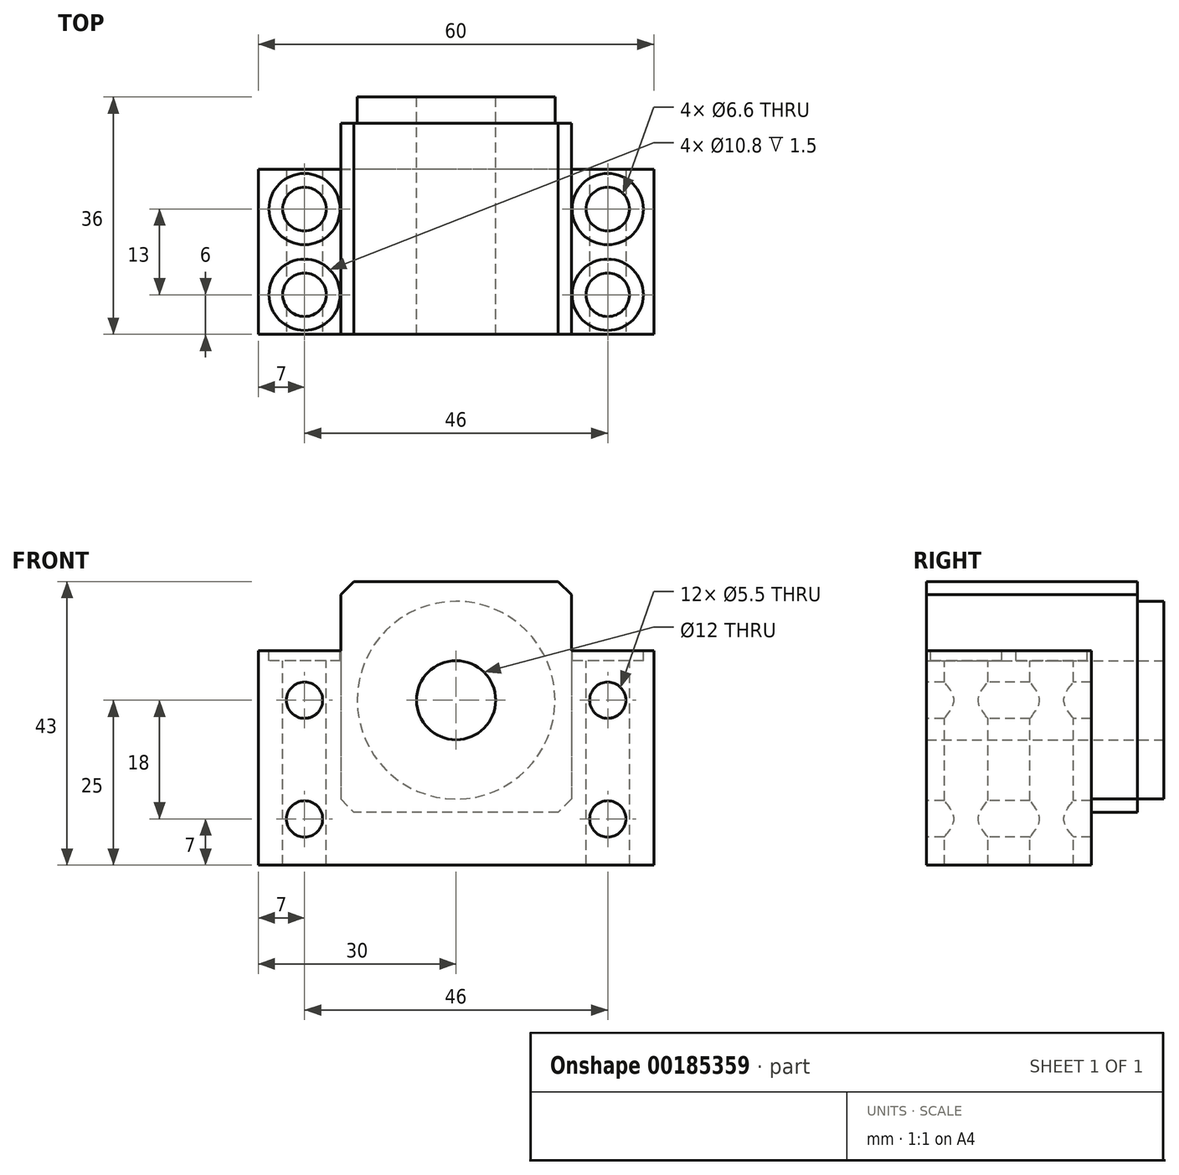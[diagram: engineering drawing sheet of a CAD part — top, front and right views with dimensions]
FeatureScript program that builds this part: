
annotation { "Feature Type Name" : "Feature", "Feature Type Description" : "" }
export const myFeature = defineFeature(function(context is Context, id is Id, definition is map)
    precondition{}
    {
        {
            var Q0;
            Q0=qCreatedBy(makeId("Front.planeOp"),FACE);
            var sketch = newSketch(context, id + "F8", { "sketchPlane" : qUnion([Q0])});
            skLineSegment(sketch, "E0.bottom", {"start": v(30, 16.25) * mm, "end": v(-30, 16.25) * mm});
            skLineSegment(sketch, "E0.top", {"start": v(30, -16.25) * mm, "end": v(-30, -16.25) * mm});
            skLineSegment(sketch, "E0.left", {"start": v(30, 16.25) * mm, "end": v(30, -16.25) * mm});
            skLineSegment(sketch, "E0.right", {"start": v(-30, 16.25) * mm, "end": v(-30, -16.25) * mm});
            skPoint(sketch, "E0.middle", {"position": v(0, 0) * mm});
            skSolve(sketch);
        }
        {
            var Q0;
            Q0=makeQuery(id+"F8.imprint","IMPRINT",FACE,{"disambiguationData":[TD([[makeQuery(id+"F8.imprint","IMPRINT",EDGE,{"derivedFrom":sQuery(id+"F8.wireOp",EDGE,"E0.bottom")}),1.0]])]});
            extrude(context, id + "F9", {"entities" : qUnion([Q0]), "oppositeDirection" : true, "depth" : 25 * mm});
        }
        {
            var Q0;
            Q0=qCreatedBy(makeId("Front.planeOp"),FACE);
            var sketch = newSketch(context, id + "F0", { "sketchPlane" : qUnion([Q0])});
            skLineSegment(sketch, "E1.bottom", {"start": v(17.5, 26.75) * mm, "end": v(-17.5, 26.75) * mm});
            skLineSegment(sketch, "E1.top", {"start": v(17.5, -8.25) * mm, "end": v(-17.5, -8.25) * mm});
            skLineSegment(sketch, "E1.left", {"start": v(17.5, 26.75) * mm, "end": v(17.5, -8.25) * mm});
            skLineSegment(sketch, "E1.right", {"start": v(-17.5, 26.75) * mm, "end": v(-17.5, -8.25) * mm});
            skPoint(sketch, "E1.middle", {"position": v(0, 9.25) * mm});
            skSolve(sketch);
        }
        {
            var Q0;
            Q0=makeQuery(id+"F0.imprint","IMPRINT",FACE,{"disambiguationData":[TD([[makeQuery(id+"F0.imprint","IMPRINT",EDGE,{"derivedFrom":sQuery(id+"F0.wireOp",EDGE,"E1.bottom")}),1.0]])]});
            extrude(context, id + "F10", {"entities" : qUnion([Q0]), "operationType" : NewBodyOperationType.ADD, "oppositeDirection" : true, "depth" : 32 * mm});
        }
        {
            var Q0;
            Q0=makeQuery(id+"F10.opExtrude","CAP_FACE",FACE,{"disambiguationData":[OSD([sQuery(id+"F0.wireOp",EDGE,"E1.bottom"),sQuery(id+"F0.wireOp",EDGE,"E1.top"),sQuery(id+"F0.wireOp",EDGE,"E1.left"),sQuery(id+"F0.wireOp",EDGE,"E1.right")])],"isStart":false});
            var sketch = newSketch(context, id + "F1", { "sketchPlane" : qUnion([Q0])});
            skCircle(sketch, "E2", {"center": v(0, 8.75) * mm, "radius": 6 * mm});
            skSolve(sketch);
        }
        {
            var Q0;
            Q0=makeQuery(id+"F1.imprint","IMPRINT",FACE,{"disambiguationData":[TD([[makeQuery(id+"F1.imprint","IMPRINT",EDGE,{"derivedFrom":sQuery(id+"F1.wireOp",EDGE,"E2")}),1.0]])]});
            var Q1;
            Q1=sQuery(id+"F1.wireOp",EDGE,"E2");
            extrude(context, id + "F11", {"entities" : qUnion([Q0]), "operationType" : NewBodyOperationType.REMOVE, "surfaceEntities" : qUnion([Q1]), "endBound" : BoundingType.THROUGH_ALL, "oppositeDirection" : true, "depth" : 25 * mm});
        }
        {
            var Q0;
            Q0=makeQuery(id+"F10.opExtrude","SWEPT_EDGE",EDGE,{"disambiguationData":[OSD([sQuery(id+"F0.wireOp",EDGE,"E1.bottom"),sQuery(id+"F0.wireOp",EDGE,"E1.right")])]});
            var Q1;
            Q1=makeQuery(id+"F10.opExtrude","SWEPT_EDGE",EDGE,{"disambiguationData":[OSD([sQuery(id+"F0.wireOp",EDGE,"E1.bottom"),sQuery(id+"F0.wireOp",EDGE,"E1.left")])]});
            chamfer(context, id + "F2", {"entities" : qUnion([Q0, Q1]), "width" : 2 * mm, "tangentPropagation" : true});
        }
        {
            var Q0;
            Q0=qCreatedBy(makeId("Front.planeOp"),FACE);
            var sketch = newSketch(context, id + "F3", { "sketchPlane" : qUnion([Q0])});
            skPoint(sketch, "E3.middle", {"position": v(0, -0.25) * mm});
            skCircle(sketch, "E4", {"center": v(23, 8.75) * mm, "radius": 2.75 * mm});
            skCircle(sketch, "E5", {"center": v(23, -9.25) * mm, "radius": 2.75 * mm});
            skCircle(sketch, "E6", {"center": v(-23, -9.25) * mm, "radius": 2.75 * mm});
            skCircle(sketch, "E7", {"center": v(-23, 8.75) * mm, "radius": 2.75 * mm});
            skSolve(sketch);
        }
        {
            var Q0;
            Q0=makeQuery(id+"F3.imprint","IMPRINT",FACE,{"disambiguationData":[TD([[makeQuery(id+"F3.imprint","IMPRINT",EDGE,{"derivedFrom":sQuery(id+"F3.wireOp",EDGE,"E5")}),1.0]])]});
            var Q1;
            Q1=makeQuery(id+"F3.imprint","IMPRINT",FACE,{"disambiguationData":[TD([[makeQuery(id+"F3.imprint","IMPRINT",EDGE,{"derivedFrom":sQuery(id+"F3.wireOp",EDGE,"E4")}),1.0]])]});
            var Q2;
            Q2=makeQuery(id+"F3.imprint","IMPRINT",FACE,{"disambiguationData":[TD([[makeQuery(id+"F3.imprint","IMPRINT",EDGE,{"derivedFrom":sQuery(id+"F3.wireOp",EDGE,"E7")}),1.0]])]});
            var Q3;
            Q3=makeQuery(id+"F3.imprint","IMPRINT",FACE,{"disambiguationData":[TD([[makeQuery(id+"F3.imprint","IMPRINT",EDGE,{"derivedFrom":sQuery(id+"F3.wireOp",EDGE,"E6")}),1.0]])]});
            extrude(context, id + "F12", {"entities" : qUnion([Q0, Q1, Q2, Q3]), "operationType" : NewBodyOperationType.REMOVE, "endBound" : BoundingType.THROUGH_ALL, "oppositeDirection" : true, "depth" : 25 * mm});
        }
        {
            var Q0;
            Q0=makeQuery(id+"F10.opExtrude","SWEPT_EDGE",EDGE,{"disambiguationData":[OSD([sQuery(id+"F0.wireOp",EDGE,"E1.top"),sQuery(id+"F0.wireOp",EDGE,"E1.right")])]});
            var Q1;
            Q1=makeQuery(id+"F10.opExtrude","SWEPT_EDGE",EDGE,{"disambiguationData":[OSD([sQuery(id+"F0.wireOp",EDGE,"E1.top"),sQuery(id+"F0.wireOp",EDGE,"E1.left")])]});
            chamfer(context, id + "F4", {"entities" : qUnion([Q0, Q1]), "width" : 2 * mm, "tangentPropagation" : true});
        }
        {
            var Q0;
            {var subQ0=sQuery(id+"F8.wireOp",EDGE,"E0.right");var subQ3=sQuery(id+"F8.wireOp",EDGE,"E0.bottom");Q0=makeQuery(id+"F10.boolean.opBoolean","SPLIT",FACE,{"disambiguationData":[TD([makeQuery(id+"F9.opExtrude","SWEPT_FACE",FACE,{"disambiguationData":[OSD([subQ0])]})])],"derivedFrom":makeQuery(id+"F9.opExtrude","SWEPT_FACE",FACE,{"disambiguationData":[OSD([subQ3])]})});}
            var sketch = newSketch(context, id + "F5", { "sketchPlane" : qUnion([Q0])});
            skCircle(sketch, "E8", {"center": v(-23, 19) * mm, "radius": 3.3 * mm});
            skCircle(sketch, "E9", {"center": v(-23, 6) * mm, "radius": 3.3 * mm});
            skCircle(sketch, "E10.MirrorC", {"center": v(23, 19) * mm, "radius": 3.3 * mm});
            skCircle(sketch, "E11.MirrorC", {"center": v(23, 6) * mm, "radius": 3.3 * mm});
            skPoint(sketch, "E12.start.orphan", {"position": v(0, 35.82) * mm});
            skSolve(sketch);
        }
        {
            var Q0;
            Q0=sQuery(id+"F5.wireOp",VERTEX,"E9.center");
            var Q1;
            Q1=sQuery(id+"F5.wireOp",VERTEX,"E8.center");
            var Q2;
            Q2=sQuery(id+"F5.wireOp",VERTEX,"E11.MirrorC.center");
            var Q3;
            Q3=sQuery(id+"F5.wireOp",VERTEX,"E10.MirrorC.center");
            var Q4;
            Q4=makeQuery(id+"F9.opExtrude","SWEPT_BODY",BODY,{"disambiguationData":[OSD([sQuery(id+"F8.wireOp",EDGE,"E0.bottom"),sQuery(id+"F8.wireOp",EDGE,"E0.top"),sQuery(id+"F8.wireOp",EDGE,"E0.left"),sQuery(id+"F8.wireOp",EDGE,"E0.right")])]});
            hole(context, id + "F6", {"style" : HoleStyle.C_BORE, "endStyle" : HoleEndStyle.THROUGH, "holeDiameter" : 6.6 * mm, "cBoreDiameter" : 10.8 * mm, "cBoreDepth" : 1.5 * mm, "locations" : qUnion([Q0, Q1, Q2, Q3]), "scope" : qUnion([Q4]), "isTappedThrough" : true});
        }
        {
            var Q0;
            Q0=makeQuery(id+"F10.opExtrude","CAP_FACE",FACE,{"disambiguationData":[OSD([sQuery(id+"F0.wireOp",EDGE,"E1.bottom"),sQuery(id+"F0.wireOp",EDGE,"E1.top"),sQuery(id+"F0.wireOp",EDGE,"E1.left"),sQuery(id+"F0.wireOp",EDGE,"E1.right")])],"isStart":false});
            var sketch = newSketch(context, id + "F13", { "sketchPlane" : qUnion([Q0])});
            skPoint(sketch, "E13.middle", {"position": v(0, 8.75) * mm});
            skPoint(sketch, "E13.right.end.orphan", {"position": v(-18.85, -10.1) * mm});
            skPoint(sketch, "E13.right.start.orphan", {"position": v(-18.85, 27.6) * mm});
            skPoint(sketch, "E13.left.end.orphan", {"position": v(18.85, -10.1) * mm});
            skPoint(sketch, "E13.left.start.orphan", {"position": v(18.85, 27.6) * mm});
            skCircle(sketch, "E14", {"center": v(0, 8.75) * mm, "radius": 15 * mm});
            skSolve(sketch);
        }
        {
            var Q0;
            Q0=makeQuery(id+"F13.imprint","IMPRINT",FACE,{"disambiguationData":[TD([[makeQuery(id+"F13.imprint","IMPRINT",EDGE,{"derivedFrom":sQuery(id+"F13.wireOp",EDGE,"E14")}),1.0]])]});
            var Q1;
            Q1=sQuery(id+"F13.wireOp",EDGE,"E14");
            extrude(context, id + "F7", {"entities" : qUnion([Q0]), "operationType" : NewBodyOperationType.ADD, "surfaceEntities" : qUnion([Q1]), "depth" : 4 * mm});
        }
    });
